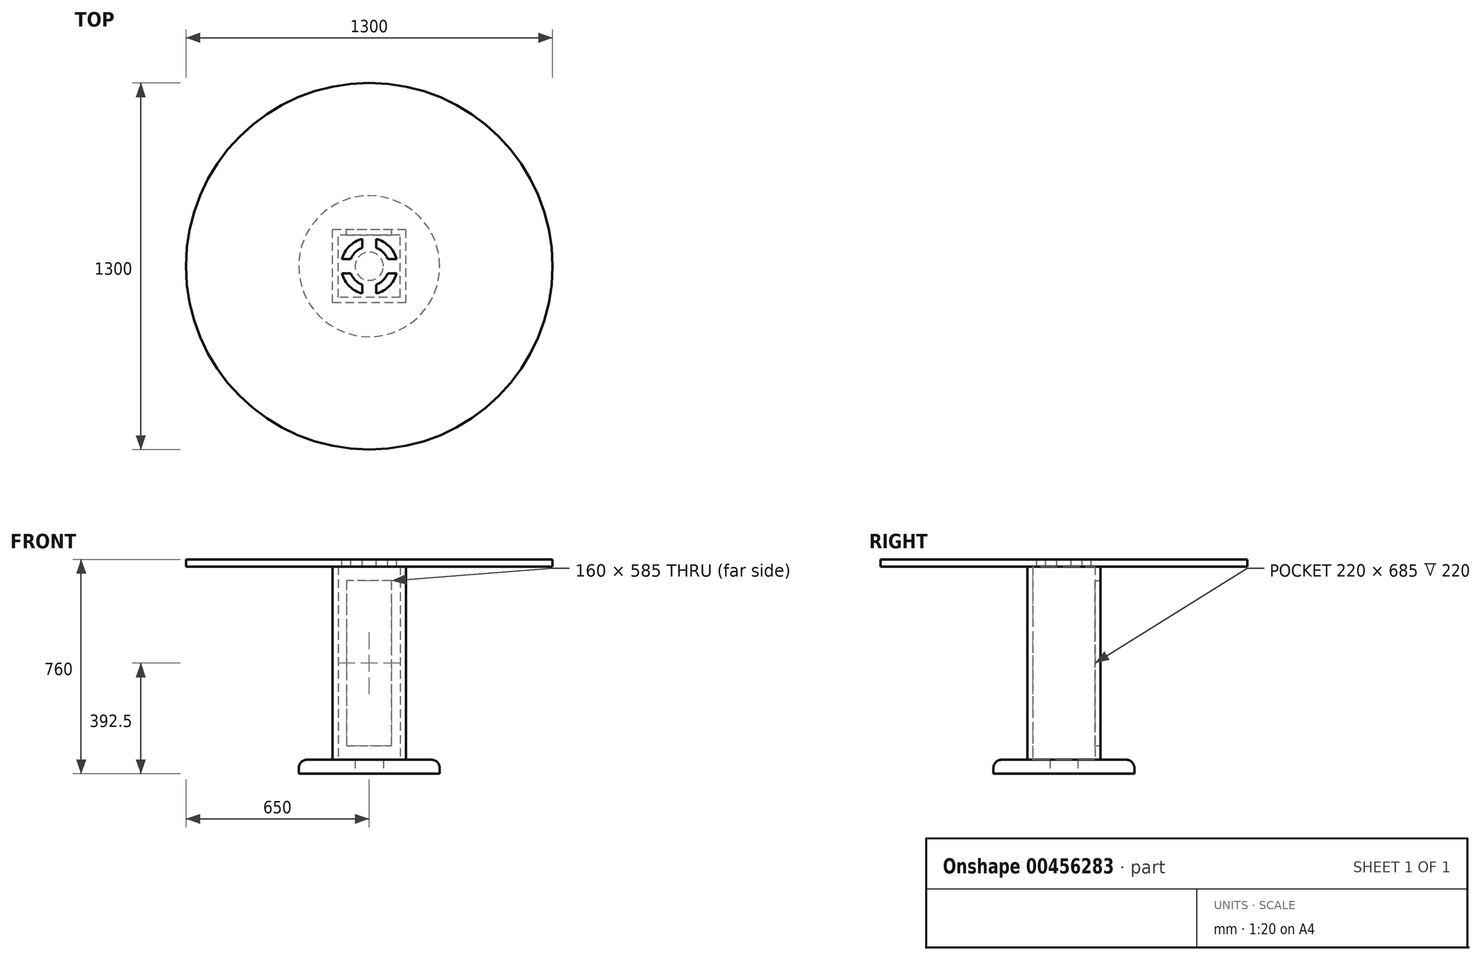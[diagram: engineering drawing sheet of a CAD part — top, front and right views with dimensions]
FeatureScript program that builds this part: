
annotation { "Feature Type Name" : "Feature", "Feature Type Description" : "" }
export const myFeature = defineFeature(function(context is Context, id is Id, definition is map)
    precondition{}
    {
        {
            var Q0;
            Q0=qCreatedBy(makeId("Top.planeOp"),FACE);
            var sketch = newSketch(context, id + "F0", { "sketchPlane" : qUnion([Q0])});
            skCircle(sketch, "E0", {"center": v(0, 0) * mm, "radius": 250 * mm});
            skSolve(sketch);
        }
        {
            var Q0;
            Q0=makeQuery(id+"F0.imprint","IMPRINT",FACE,{"disambiguationData":[TD([[makeQuery(id+"F0.imprint","IMPRINT",EDGE,{"derivedFrom":sQuery(id+"F0.wireOp",EDGE,"E0")}),1.0]])]});
            extrude(context, id + "F1", {"entities" : qUnion([Q0]), "depth" : 50 * mm});
        }
        {
            var Q0;
            Q0=makeQuery(id+"F1.opExtrude","CAP_EDGE",EDGE,{"disambiguationData":[OSD([sQuery(id+"F0.wireOp",EDGE,"E0")])],"isStart":false});
            fillet(context, id + "F2", {"entities" : qUnion([Q0]), "radius" : 30 * mm, "tangentPropagation" : true, "allowEdgeOverflow" : false});
        }
        {
            var Q0;
            Q0=makeQuery(id+"F1.opExtrude","CAP_FACE",FACE,{"disambiguationData":[OSD([sQuery(id+"F0.wireOp",EDGE,"E0")])],"isStart":false});
            var sketch = newSketch(context, id + "F3", { "sketchPlane" : qUnion([Q0])});
            skLineSegment(sketch, "E1.bottom", {"start": v(110, -110) * mm, "end": v(-110, -110) * mm});
            skLineSegment(sketch, "E1.top", {"start": v(110, 110) * mm, "end": v(-110, 110) * mm});
            skLineSegment(sketch, "E1.left", {"start": v(110, -110) * mm, "end": v(110, 110) * mm});
            skLineSegment(sketch, "E1.right", {"start": v(-110, -110) * mm, "end": v(-110, 110) * mm});
            skPoint(sketch, "E1.middle", {"position": v(0, 0) * mm});
            skLineSegment(sketch, "E2.0", {"start": v(130, 130) * mm, "end": v(-130, 130) * mm});
            skLineSegment(sketch, "E2.1", {"start": v(130, -130) * mm, "end": v(130, 130) * mm});
            skLineSegment(sketch, "E2.2", {"start": v(130, -130) * mm, "end": v(-130, -130) * mm});
            skLineSegment(sketch, "E2.3", {"start": v(-130, -130) * mm, "end": v(-130, 130) * mm});
            skSolve(sketch);
        }
        {
            var Q0;
            Q0 = qSketchRegion(id + "F3", true);
            extrude(context, id + "F4", {"entities" : qUnion([Q0]), "operationType" : NewBodyOperationType.ADD, "depth" : 685 * mm});
        }
        {
            var Q0;
            {var subQ0=sQuery(id+"F3.wireOp",EDGE,"E2.2");var subQ2=sQuery(id+"F3.wireOp",EDGE,"E2.1");var subQ4=sQuery(id+"F3.wireOp",EDGE,"E1.left");var subQ5=makeQuery(id+"F4.opExtrude","SWEPT_FACE",FACE,{"disambiguationData":[OSD([subQ4])]});var subQ6=sQuery(id+"F3.wireOp",EDGE,"E1.bottom");var subQ7=makeQuery(id+"F4.opExtrude","SWEPT_FACE",FACE,{"disambiguationData":[OSD([subQ6])]});var subQ8=sQuery(id+"F3.wireOp",EDGE,"E2.0");var subQ9=sQuery(id+"F3.wireOp",EDGE,"E1.top");var subQ10=makeQuery(id+"F4.opExtrude","CAP_FACE",FACE,{"disambiguationData":[OSD([subQ6,subQ9,subQ4,sQuery(id+"F3.wireOp",EDGE,"E1.right"),subQ8,subQ2,subQ0,sQuery(id+"F3.wireOp",EDGE,"E2.3")])],"isStart":false});Q0=makeQuery(id+"FZugcAsQUtjeGXy_1.boolean.opBoolean","SPLIT",FACE,{"disambiguationData":[TD([subQ7])],"derivedFrom":makeQuery(id+"FC2nL2Hn6jOOdrO_1.boolean.opBoolean","SPLIT",FACE,{"disambiguationData":[TD([subQ5])],"derivedFrom":subQ10})});}
            var sketch = newSketch(context, id + "F5", { "sketchPlane" : qUnion([Q0])});
            skCircle(sketch, "E3", {"center": v(0, 0) * mm, "radius": 650 * mm});
            skSolve(sketch);
        }
        {
            var Q0;
            Q0=makeQuery(id+"F5.imprint","IMPRINT",FACE,{"disambiguationData":[TD([[makeQuery(id+"F5.imprint","IMPRINT",EDGE,{"derivedFrom":sQuery(id+"F5.wireOp",EDGE,"E3")}),1.0]])]});
            var Q1;
            {var subQ0=sQuery(id+"F3.wireOp",EDGE,"E1.bottom");var subQ5=sQuery(id+"F3.wireOp",EDGE,"E1.left");var subQ7=makeQuery(id+"F4.opExtrude","SWEPT_FACE",FACE,{"disambiguationData":[OSD([subQ5])]});Q1=makeQuery(id+"F5.imprint","IMPRINT",FACE,{"disambiguationData":[TD([[makeQuery(id+"F5.imprint","IMPRINT",EDGE,{"derivedFrom":makeQuery(id+"FC2nL2Hn6jOOdrO_1.boolean.opBoolean","SPLIT",EDGE,{"disambiguationData":[TD([subQ7])],"derivedFrom":makeQuery(id+"F4.opExtrude","CAP_EDGE",EDGE,{"disambiguationData":[OSD([subQ0])],"isStart":false})})}),1.0]])]});}
            var Q2;
            Q2=makeQuery(id+"F5.imprint","IMPRINT",FACE,{"disambiguationData":[TD([[makeQuery(id+"F5.imprint","IMPRINT",EDGE,{"derivedFrom":makeQuery(id+"F4.opExtrude","CAP_EDGE",EDGE,{"disambiguationData":[OSD([sQuery(id+"F3.wireOp",EDGE,"E1.bottom")])],"isStart":false})}),-1.0]])]});
            extrude(context, id + "F6", {"entities" : qUnion([Q0, Q1, Q2]), "operationType" : NewBodyOperationType.ADD, "depth" : 25 * mm});
        }
        {
            var Q0;
            Q0=makeQuery(id+"F6.opExtrude","CAP_FACE",FACE,{"disambiguationData":[OSD([sQuery(id+"F5.wireOp",EDGE,"E3")])],"isStart":false});
            var sketch = newSketch(context, id + "F7", { "sketchPlane" : qUnion([Q0])});
            skCircle(sketch, "E4", {"center": v(0, 0) * mm, "radius": 100 * mm});
            skCircle(sketch, "E5.0", {"center": v(0, 0) * mm, "radius": 70 * mm});
            skLineSegment(sketch, "E6", {"start": v(0, 100) * mm, "end": v(0, -100) * mm});
            skLineSegment(sketch, "E7", {"start": v(100, 0) * mm, "end": v(-100, 0) * mm});
            skArc(sketch, "E8.0.startCap", {"start": v(-25, 100) * mm, "mid": v(0, 125) * mm, "end": v(25, 100) * mm});
            skArc(sketch, "E8.0.endCap", {"start": v(25, -100) * mm, "mid": v(0, -125) * mm, "end": v(-25, -100) * mm});
            skLineSegment(sketch, "E8.0.left", {"start": v(25, 100) * mm, "end": v(25, -100) * mm});
            skLineSegment(sketch, "E8.0.right", {"start": v(-25, 100) * mm, "end": v(-25, -100) * mm});
            skArc(sketch, "E8.1.startCap", {"start": v(100, 25) * mm, "mid": v(125, 0) * mm, "end": v(100, -25) * mm});
            skArc(sketch, "E8.1.endCap", {"start": v(-100, -25) * mm, "mid": v(-125, 0) * mm, "end": v(-100, 25) * mm});
            skLineSegment(sketch, "E8.1.left", {"start": v(100, -25) * mm, "end": v(-100, -25) * mm});
            skLineSegment(sketch, "E8.1.right", {"start": v(100, 25) * mm, "end": v(-100, 25) * mm});
            skSolve(sketch);
        }
        {
            var Q0;
            {var subQ0=sQuery(id+"F7.wireOp",EDGE,"E8.1.right");var subQ1=sQuery(id+"F7.wireOp",EDGE,"E4");var subQ2=makeQuery(id+"F7.imprint","INTERSECT",VERTEX,{"disambiguationData":[OD(0.0)],"derivedFrom":[subQ1,subQ0]});Q0=makeQuery(id+"F7.imprint","IMPRINT",FACE,{"disambiguationData":[TD([[makeQuery(id+"F7.imprint","IMPRINT",EDGE,{"disambiguationData":[TD([[subQ2,-1.0]])],"derivedFrom":subQ1}),1.0]])]});}
            var Q1;
            {var subQ0=sQuery(id+"F7.wireOp",EDGE,"E8.0.right");var subQ1=sQuery(id+"F7.wireOp",EDGE,"E4");var subQ2=makeQuery(id+"F7.imprint","INTERSECT",VERTEX,{"disambiguationData":[OD(0.0)],"derivedFrom":[subQ1,subQ0]});Q1=makeQuery(id+"F7.imprint","IMPRINT",FACE,{"disambiguationData":[TD([[makeQuery(id+"F7.imprint","IMPRINT",EDGE,{"disambiguationData":[TD([[subQ2,-1.0]])],"derivedFrom":subQ1}),1.0]])]});}
            var Q2;
            {var subQ0=sQuery(id+"F7.wireOp",EDGE,"E8.1.left");var subQ1=sQuery(id+"F7.wireOp",EDGE,"E4");var subQ2=makeQuery(id+"F7.imprint","INTERSECT",VERTEX,{"disambiguationData":[OD(0.0)],"derivedFrom":[subQ1,subQ0]});Q2=makeQuery(id+"F7.imprint","IMPRINT",FACE,{"disambiguationData":[TD([[makeQuery(id+"F7.imprint","IMPRINT",EDGE,{"disambiguationData":[TD([[subQ2,-1.0]])],"derivedFrom":subQ1}),1.0]])]});}
            var Q3;
            {var subQ0=sQuery(id+"F7.wireOp",EDGE,"E8.0.left");var subQ1=sQuery(id+"F7.wireOp",EDGE,"E4");var subQ2=makeQuery(id+"F7.imprint","INTERSECT",VERTEX,{"disambiguationData":[OD(1.0)],"derivedFrom":[subQ1,subQ0]});Q3=makeQuery(id+"F7.imprint","IMPRINT",FACE,{"disambiguationData":[TD([[makeQuery(id+"F7.imprint","IMPRINT",EDGE,{"disambiguationData":[TD([[subQ2,-1.0]])],"derivedFrom":subQ1}),1.0]])]});}
            var Q4;
            {var subQ0=sQuery(id+"F7.wireOp",EDGE,"E8.1.right");var subQ1=sQuery(id+"F7.wireOp",EDGE,"E4");var subQ2=makeQuery(id+"F7.imprint","INTERSECT",VERTEX,{"disambiguationData":[OD(0.0)],"derivedFrom":[subQ1,subQ0]});Q4=makeQuery(id+"F7.imprint","IMPRINT",FACE,{"disambiguationData":[TD([[makeQuery(id+"F7.imprint","IMPRINT",EDGE,{"disambiguationData":[TD([[subQ2,-1.0]])],"derivedFrom":subQ1}),1.0]])]});}
            extrude(context, id + "F8", {"entities" : qUnion([Q0, Q1, Q2, Q3, Q4]), "operationType" : NewBodyOperationType.REMOVE, "oppositeDirection" : true, "depth" : 100 * mm});
        }
        {
            var Q0;
            Q0=makeQuery(id+"F4.opExtrude","SWEPT_FACE",FACE,{"disambiguationData":[OSD([sQuery(id+"F3.wireOp",EDGE,"E2.0")])]});
            var sketch = newSketch(context, id + "F9", { "sketchPlane" : qUnion([Q0])});
            skLineSegment(sketch, "E9.0", {"start": v(-80, 100) * mm, "end": v(80, 100) * mm});
            skLineSegment(sketch, "E9.1", {"start": v(-80, 685) * mm, "end": v(-80, 100) * mm});
            skLineSegment(sketch, "E9.2", {"start": v(80, 685) * mm, "end": v(-80, 685) * mm});
            skLineSegment(sketch, "E9.3", {"start": v(80, 100) * mm, "end": v(80, 685) * mm});
            skSolve(sketch);
        }
        {
            var Q0;
            Q0 = qSketchRegion(id + "F9", true);
            var Q1;
            Q1=makeQuery(id+"F9.imprint","IMPRINT",FACE,{"disambiguationData":[TD([[makeQuery(id+"F9.imprint","IMPRINT",EDGE,{"derivedFrom":sQuery(id+"F9.wireOp",EDGE,"E9.0")}),1.0]])]});
            extrude(context, id + "F10", {"entities" : qUnion([Q0, Q1]), "operationType" : NewBodyOperationType.REMOVE, "oppositeDirection" : true, "depth" : 40 * mm});
        }
        {
            var Q0;
            Q0=makeQuery(id+"F1.opExtrude","CAP_FACE",FACE,{"disambiguationData":[OSD([sQuery(id+"F0.wireOp",EDGE,"E0")])],"isStart":true});
            var sketch = newSketch(context, id + "F11", { "sketchPlane" : qUnion([Q0])});
            skCircle(sketch, "E10", {"center": v(0, 0) * mm, "radius": 50 * mm});
            skSolve(sketch);
        }
        {
            var Q0;
            Q0=makeQuery(id+"F11.imprint","IMPRINT",FACE,{"disambiguationData":[TD([[makeQuery(id+"F11.imprint","IMPRINT",EDGE,{"derivedFrom":sQuery(id+"F11.wireOp",EDGE,"E10")}),1.0]])]});
            extrude(context, id + "F12", {"entities" : qUnion([Q0]), "operationType" : NewBodyOperationType.REMOVE, "oppositeDirection" : true, "depth" : 50 * mm});
        }
    });
